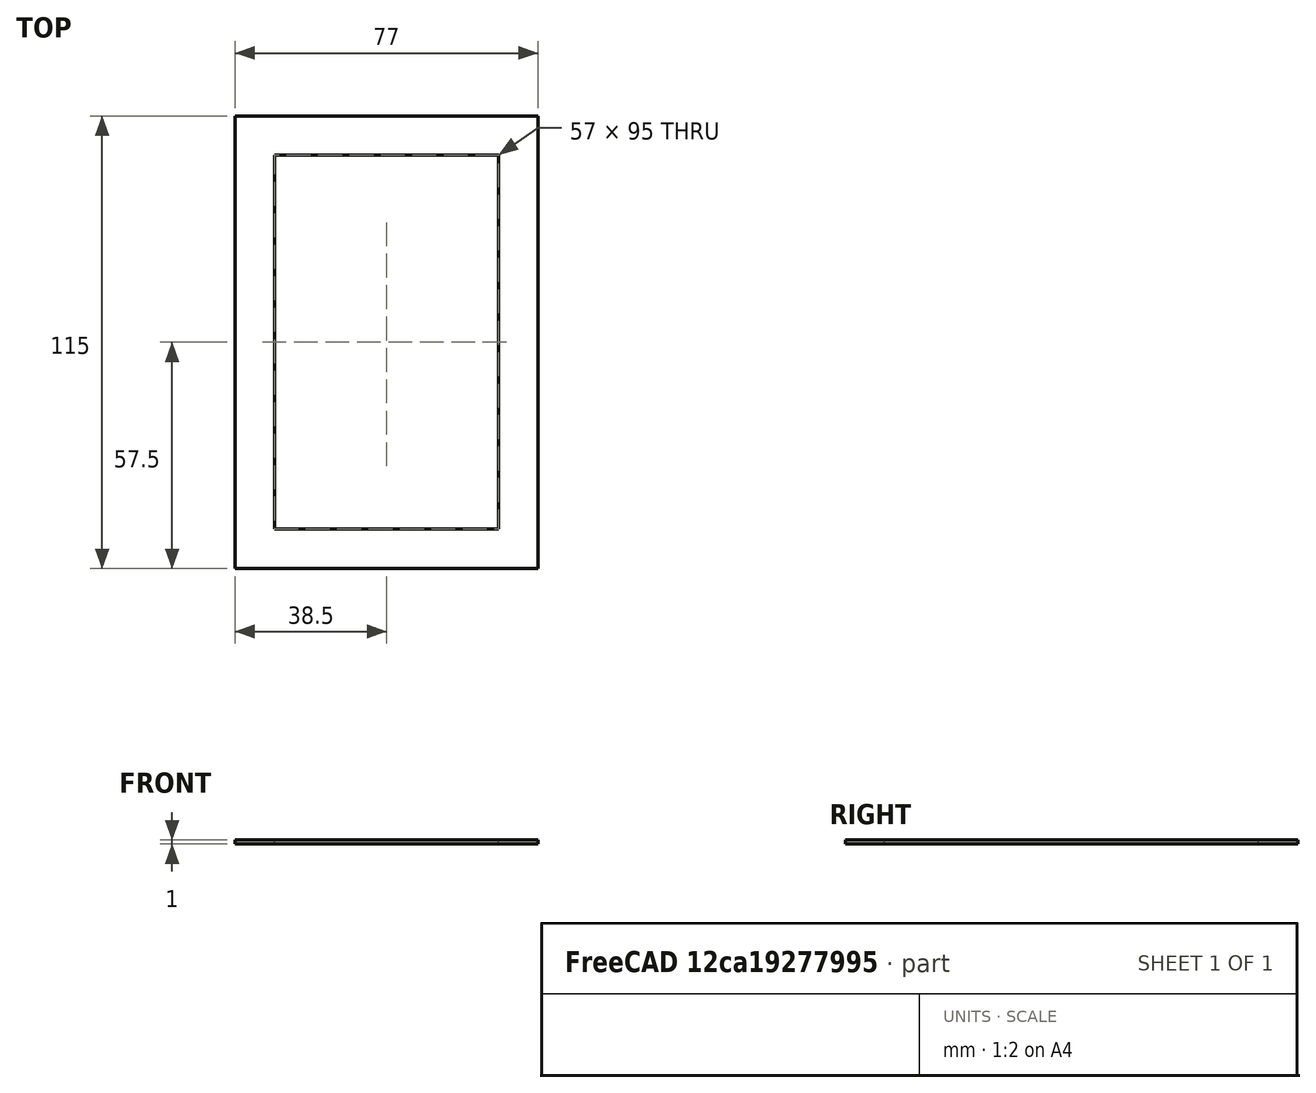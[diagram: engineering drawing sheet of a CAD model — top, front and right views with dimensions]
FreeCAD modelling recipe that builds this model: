
FCSTD DOCUMENT  (FreeCAD 1.0R39109 (Git))
Label: wall plate template
License: All rights reserved
LicenseURL: https://en.wikipedia.org/wiki/All_rights_reserved
objects: Sketcher::SketchObject×1, PartDesign::Pad×1, PartDesign::Body×1
note: 6 computed .brp shape members not serialized (recipe doc carries the construction recipe); baked Part::Feature solids carry a one-line shape summary decoded from their .brp

FEATURE [Sketcher::SketchObject] Sketch
  ArcFitTolerance = 1e-06
  AttachmentSupport = -> [XY_Plane]
  FullyConstrained = true
  MakeInternals = false
  MapMode = 5
  sketch-geometry (10):
    g0: LineSegment StartX=-28.5 StartY=47.5 StartZ=0 EndX=-28.5 EndY=-47.5 EndZ=0
    g1: LineSegment StartX=-28.5 StartY=-47.5 StartZ=0 EndX=28.5 EndY=-47.5 EndZ=0
    g2: LineSegment StartX=28.5 StartY=-47.5 StartZ=0 EndX=28.5 EndY=47.5 EndZ=0
    g3: LineSegment StartX=28.5 StartY=47.5 StartZ=0 EndX=-28.5 EndY=47.5 EndZ=0
    g4: GeomPoint [constr] X=0 Y=0 Z=0
    g5: LineSegment StartX=-38.5 StartY=57.5 StartZ=0 EndX=-38.5 EndY=-57.5 EndZ=0
    g6: LineSegment StartX=-38.5 StartY=-57.5 StartZ=0 EndX=38.5 EndY=-57.5 EndZ=0
    g7: LineSegment StartX=38.5 StartY=-57.5 StartZ=0 EndX=38.5 EndY=57.5 EndZ=0
    g8: LineSegment StartX=38.5 StartY=57.5 StartZ=0 EndX=-38.5 EndY=57.5 EndZ=0
    g9: GeomPoint [constr] X=0 Y=0 Z=0
  constraints (24):
    c: Coincident(g0,g1)
    c: Coincident(g1,g2)
    c: Coincident(g2,g3)
    c: Coincident(g3,g0)
    c: Vertical(g0)
    c: Vertical(g2)
    c: Horizontal(g1)
    c: Horizontal(g3)
    c: Symmetric(g2,g0,g4)
    c: Coincident(g4,g-1)
    c: Coincident(g5,g6)
    c: Coincident(g6,g7)
    c: Coincident(g7,g8)
    c: Coincident(g8,g5)
    c: Vertical(g5)
    c: Vertical(g7)
    c: Horizontal(g6)
    c: Horizontal(g8)
    c: Symmetric(g7,g5,g9)
    c: Coincident(g9,g4)
    c: DistanceY(g0,g5) = 10
    c: DistanceX(g5,g0) = 10
    c: DistanceY(g0,g0) = 95
    c: DistanceX(g3,g3) = 57
FEATURE [PartDesign::Pad] Pad
  Direction = (0,0,1)
  Length = 1
  Length2 = 10
  Profile = -> Sketch
  ReferenceAxis = -> Sketch [N_Axis]
  Refine = true
  Suppressed = false
  Type = 0
FEATURE [PartDesign::Body] Body
  AllowCompound = false
  Group = -> [Sketch,Pad]
  Origin = -> Origin
  Tip = -> Pad
